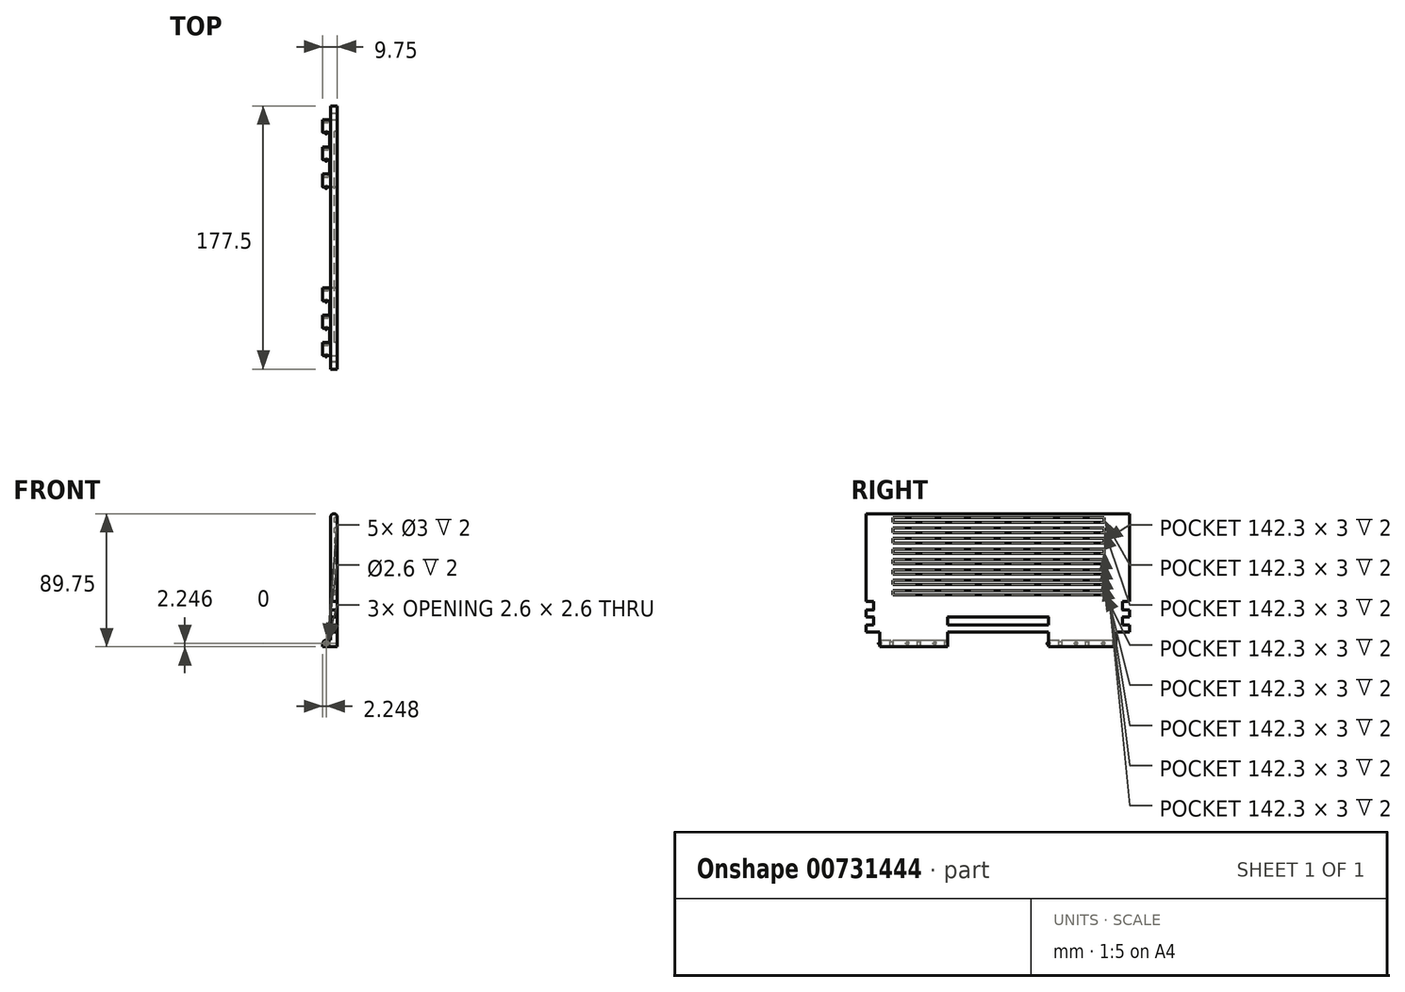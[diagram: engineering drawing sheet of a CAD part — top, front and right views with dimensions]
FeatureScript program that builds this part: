
annotation { "Feature Type Name" : "Feature", "Feature Type Description" : "" }
export const myFeature = defineFeature(function(context is Context, id is Id, definition is map)
    precondition{}
    {
        {
            var Q0;
            Q0=qCreatedBy(makeId("Front.planeOp"),FACE);
            var sketch = newSketch(context, id + "F0", { "sketchPlane" : qUnion([Q0])});
            skLineSegment(sketch, "E0", {"start": v(-23.3, -0.71) * mm, "end": v(-23.3, 86.79) * mm});
            skLineSegment(sketch, "E1", {"start": v(-25.55, 89.04) * mm, "end": v(-25.55, 89.04) * mm});
            skLineSegment(sketch, "E2", {"start": v(-27.8, 86.79) * mm, "end": v(-27.8, 29.79) * mm});
            skLineSegment(sketch, "E3", {"start": v(-33.05, -0.71) * mm, "end": v(-30.8, -0.71) * mm});
            skPoint(sketch, "E4.visualSharp", {"position": v(-28.55, -0.71) * mm});
            skLineSegment(sketch, "E5", {"start": v(-33.05, -0.71) * mm, "end": v(-23.3, -0.71) * mm});
            skLineSegment(sketch, "E6", {"start": v(-33.05, 1.54) * mm, "end": v(-33.05, -0.71) * mm});
            skLineSegment(sketch, "E7", {"start": v(-30.8, 3.79) * mm, "end": v(-27.8, 3.79) * mm});
            skPoint(sketch, "E8.visualSharp", {"position": v(-33.05, 3.79) * mm});
            skArc(sketch, "E8.filletArc", {"start": v(-30.8, 3.79) * mm, "mid": v(-32.4, 3.13) * mm, "end": v(-33.05, 1.54) * mm});
            skCircle(sketch, "E9", {"center": v(-30.8, 1.54) * mm, "radius": 1.5 * mm});
            skCircle(sketch, "E10", {"center": v(-30.8, 1.54) * mm, "radius": 1.3 * mm});
            skPoint(sketch, "E11.visualSharp", {"position": v(-27.8, 89.04) * mm});
            skArc(sketch, "E11.filletArc", {"start": v(-25.55, 89.04) * mm, "mid": v(-27.14, 88.38) * mm, "end": v(-27.8, 86.79) * mm});
            skPoint(sketch, "E12.visualSharp", {"position": v(-23.3, 89.04) * mm});
            skArc(sketch, "E12.filletArc", {"start": v(-23.3, 86.79) * mm, "mid": v(-23.96, 88.38) * mm, "end": v(-25.55, 89.04) * mm});
            skLineSegment(sketch, "E13", {"start": v(-27.8, 9.29) * mm, "end": v(-23.3, 9.29) * mm});
            skLineSegment(sketch, "E14", {"start": v(-28.35, 3.79) * mm, "end": v(-28.35, -0.71) * mm});
            skPoint(sketch, "E14.endSnap0", {"position": v(-28.18, -0.71) * mm});
            skLineSegment(sketch, "E15", {"start": v(-26.8, 24.29) * mm, "end": v(-23.3, 24.29) * mm});
            skLineSegment(sketch, "E16", {"start": v(-27.8, 29.79) * mm, "end": v(-23.3, 29.79) * mm});
            skLineSegment(sketch, "E17.filletArc", {"start": v(-27.8, 29.79) * mm, "end": v(-27.8, 29.79) * mm});
            skLineSegment(sketch, "E18", {"start": v(-27.8, 23.29) * mm, "end": v(-27.8, 20.29) * mm});
            skLineSegment(sketch, "E19", {"start": v(-27.8, 24.29) * mm, "end": v(-27.8, 29.79) * mm});
            skPoint(sketch, "E20.visualSharp", {"position": v(-27.8, 24.29) * mm});
            skArc(sketch, "E20.filletArc", {"start": v(-26.8, 24.29) * mm, "mid": v(-27.5, 24) * mm, "end": v(-27.8, 23.29) * mm});
            skLineSegment(sketch, "E21", {"start": v(-27.8, 24.29) * mm, "end": v(-27.8, 23.29) * mm});
            skLineSegment(sketch, "E22", {"start": v(-23.3, 19.29) * mm, "end": v(-26.8, 19.29) * mm});
            skLineSegment(sketch, "E23", {"start": v(-23.3, 13.89) * mm, "end": v(-27.8, 13.89) * mm});
            skArc(sketch, "E24.filletArc", {"start": v(-27.8, 20.29) * mm, "mid": v(-27.5, 19.58) * mm, "end": v(-26.8, 19.29) * mm});
            skLineSegment(sketch, "E25", {"start": v(-27.8, 13.89) * mm, "end": v(-27.8, 3.79) * mm});
            skLineSegment(sketch, "E26.filletArc", {"start": v(-27.8, 13.89) * mm, "end": v(-27.8, 13.89) * mm});
            skLineSegment(sketch, "E27", {"start": v(-27.8, 20.29) * mm, "end": v(-27.8, 13.89) * mm});
            skSolve(sketch);
        }
        {
            var Q0;
            {var subQ0=sQuery(id+"F0.wireOp",EDGE,"E13");Q0=makeQuery(id+"F0.imprint","IMPRINT",FACE,{"disambiguationData":[TD([[makeQuery(id+"F0.imprint","IMPRINT",EDGE,{"derivedFrom":subQ0}),1.0]])]});}
            var Q1;
            {var subQ3=sQuery(id+"F0.wireOp",EDGE,"E6");Q1=makeQuery(id+"F0.imprint","IMPRINT",FACE,{"disambiguationData":[TD([[makeQuery(id+"F0.imprint","IMPRINT",EDGE,{"derivedFrom":subQ3}),1.0]])]});}
            var Q2;
            {var subQ1=sQuery(id+"F0.wireOp",EDGE,"E11.filletArc");Q2=makeQuery(id+"F0.imprint","IMPRINT",FACE,{"disambiguationData":[TD([[makeQuery(id+"F0.imprint","IMPRINT",EDGE,{"derivedFrom":subQ1}),1.0]])]});}
            var Q3;
            {var subQ0=sQuery(id+"F0.wireOp",EDGE,"E15");Q3=makeQuery(id+"F0.imprint","IMPRINT",FACE,{"disambiguationData":[TD([[makeQuery(id+"F0.imprint","IMPRINT",EDGE,{"derivedFrom":subQ0}),-1.0]])]});}
            extrude(context, id + "F1", {"entities" : qUnion([Q0, Q1, Q2, Q3]), "depth" : 177.5 * mm, "offsetDistance" : 25 * mm});
        }
        {
            var Q0;
            {var subQ0=sQuery(id+"F0.wireOp",EDGE,"cf15f22d-8f12-4429-aff2-0e4cbedbb23c");Q0=makeQuery(id+"F0.imprint","IMPRINT",FACE,{"disambiguationData":[TD([[makeQuery(id+"F0.imprint","IMPRINT",EDGE,{"derivedFrom":subQ0}),1.0]])]});}
            var Q1;
            {var subQ0=sQuery(id+"F0.wireOp",EDGE,"E6");Q1=makeQuery(id+"F0.imprint","IMPRINT",FACE,{"disambiguationData":[TD([[makeQuery(id+"F0.imprint","IMPRINT",EDGE,{"derivedFrom":subQ0}),1.0]])]});}
            extrude(context, id + "F2", {"entities" : qUnion([Q0, Q1]), "operationType" : NewBodyOperationType.REMOVE, "depth" : 177.5 * mm, "offsetDistance" : 25 * mm});
        }
        {
            var Q0;
            {var subQ0=sQuery(id+"F0.wireOp",EDGE,"E6");Q0=makeQuery(id+"F0.imprint","IMPRINT",FACE,{"disambiguationData":[TD([[makeQuery(id+"F0.imprint","IMPRINT",EDGE,{"derivedFrom":subQ0}),1.0]])]});}
            var Q1;
            {var subQ0=sQuery(id+"F0.wireOp",EDGE,"cf15f22d-8f12-4429-aff2-0e4cbedbb23c");Q1=makeQuery(id+"F0.imprint","IMPRINT",FACE,{"disambiguationData":[TD([[makeQuery(id+"F0.imprint","IMPRINT",EDGE,{"derivedFrom":subQ0}),1.0]])]});}
            var Q2;
            {var subQ4=sQuery(id+"F0.wireOp",EDGE,"E13");Q2=makeQuery(id+"F0.imprint","IMPRINT",FACE,{"disambiguationData":[TD([[makeQuery(id+"F0.imprint","IMPRINT",EDGE,{"derivedFrom":subQ4}),-1.0]])]});}
            extrude(context, id + "F3", {"entities" : qUnion([Q0, Q1, Q2]), "operationType" : NewBodyOperationType.ADD, "depth" : 168.3 * mm, "offsetDistance" : 25 * mm});
        }
        {
            var Q0;
            {var subQ0=sQuery(id+"F0.wireOp",EDGE,"E6");Q0=makeQuery(id+"F0.imprint","IMPRINT",FACE,{"disambiguationData":[TD([[makeQuery(id+"F0.imprint","IMPRINT",EDGE,{"derivedFrom":subQ0}),1.0]])]});}
            extrude(context, id + "F4", {"entities" : qUnion([Q0]), "operationType" : NewBodyOperationType.REMOVE, "depth" : 159.5 * mm, "offsetDistance" : 25 * mm});
        }
        {
            var Q0;
            {var subQ0=sQuery(id+"F0.wireOp",EDGE,"cf15f22d-8f12-4429-aff2-0e4cbedbb23c");Q0=makeQuery(id+"F0.imprint","IMPRINT",FACE,{"disambiguationData":[TD([[makeQuery(id+"F0.imprint","IMPRINT",EDGE,{"derivedFrom":subQ0}),1.0]])]});}
            var Q1;
            {var subQ0=sQuery(id+"F0.wireOp",EDGE,"E6");Q1=makeQuery(id+"F0.imprint","IMPRINT",FACE,{"disambiguationData":[TD([[makeQuery(id+"F0.imprint","IMPRINT",EDGE,{"derivedFrom":subQ0}),1.0]])]});}
            var Q2;
            {var subQ4=sQuery(id+"F0.wireOp",EDGE,"E13");Q2=makeQuery(id+"F0.imprint","IMPRINT",FACE,{"disambiguationData":[TD([[makeQuery(id+"F0.imprint","IMPRINT",EDGE,{"derivedFrom":subQ4}),-1.0]])]});}
            extrude(context, id + "F5", {"entities" : qUnion([Q0, Q1, Q2]), "operationType" : NewBodyOperationType.ADD, "depth" : 149.9 * mm, "offsetDistance" : 25 * mm});
        }
        {
            var Q0;
            {var subQ0=sQuery(id+"F0.wireOp",EDGE,"E6");Q0=makeQuery(id+"F0.imprint","IMPRINT",FACE,{"disambiguationData":[TD([[makeQuery(id+"F0.imprint","IMPRINT",EDGE,{"derivedFrom":subQ0}),1.0]])]});}
            extrude(context, id + "F6", {"entities" : qUnion([Q0]), "operationType" : NewBodyOperationType.REMOVE, "depth" : 141.1 * mm, "offsetDistance" : 25 * mm});
        }
        {
            var Q0;
            {var subQ0=sQuery(id+"F0.wireOp",EDGE,"cf15f22d-8f12-4429-aff2-0e4cbedbb23c");Q0=makeQuery(id+"F0.imprint","IMPRINT",FACE,{"disambiguationData":[TD([[makeQuery(id+"F0.imprint","IMPRINT",EDGE,{"derivedFrom":subQ0}),1.0]])]});}
            var Q1;
            {var subQ0=sQuery(id+"F0.wireOp",EDGE,"E6");Q1=makeQuery(id+"F0.imprint","IMPRINT",FACE,{"disambiguationData":[TD([[makeQuery(id+"F0.imprint","IMPRINT",EDGE,{"derivedFrom":subQ0}),1.0]])]});}
            extrude(context, id + "F7", {"entities" : qUnion([Q0, Q1]), "operationType" : NewBodyOperationType.ADD, "depth" : 131.5 * mm, "offsetDistance" : 25 * mm});
        }
        {
            var Q0;
            {var subQ0=sQuery(id+"F0.wireOp",EDGE,"cf15f22d-8f12-4429-aff2-0e4cbedbb23c");Q0=makeQuery(id+"F0.imprint","IMPRINT",FACE,{"disambiguationData":[TD([[makeQuery(id+"F0.imprint","IMPRINT",EDGE,{"derivedFrom":subQ0}),1.0]])]});}
            var Q1;
            {var subQ0=sQuery(id+"F0.wireOp",EDGE,"E6");Q1=makeQuery(id+"F0.imprint","IMPRINT",FACE,{"disambiguationData":[TD([[makeQuery(id+"F0.imprint","IMPRINT",EDGE,{"derivedFrom":subQ0}),1.0]])]});}
            var Q2;
            {var subQ4=sQuery(id+"F0.wireOp",EDGE,"E13");Q2=makeQuery(id+"F0.imprint","IMPRINT",FACE,{"disambiguationData":[TD([[makeQuery(id+"F0.imprint","IMPRINT",EDGE,{"derivedFrom":subQ4}),-1.0]])]});}
            extrude(context, id + "F8", {"entities" : qUnion([Q0, Q1, Q2]), "operationType" : NewBodyOperationType.REMOVE, "depth" : 122.7 * mm, "offsetDistance" : 25 * mm});
        }
        {
            var Q0;
            {var subQ0=sQuery(id+"F0.wireOp",EDGE,"cf15f22d-8f12-4429-aff2-0e4cbedbb23c");Q0=makeQuery(id+"F0.imprint","IMPRINT",FACE,{"disambiguationData":[TD([[makeQuery(id+"F0.imprint","IMPRINT",EDGE,{"derivedFrom":subQ0}),1.0]])]});}
            var Q1;
            {var subQ0=sQuery(id+"F0.wireOp",EDGE,"E6");Q1=makeQuery(id+"F0.imprint","IMPRINT",FACE,{"disambiguationData":[TD([[makeQuery(id+"F0.imprint","IMPRINT",EDGE,{"derivedFrom":subQ0}),1.0]])]});}
            var Q2;
            {var subQ4=sQuery(id+"F0.wireOp",EDGE,"E13");Q2=makeQuery(id+"F0.imprint","IMPRINT",FACE,{"disambiguationData":[TD([[makeQuery(id+"F0.imprint","IMPRINT",EDGE,{"derivedFrom":subQ4}),-1.0]])]});}
            extrude(context, id + "F9", {"entities" : qUnion([Q0, Q1, Q2]), "operationType" : NewBodyOperationType.ADD, "depth" : 54.8 * mm, "offsetDistance" : 25 * mm});
        }
        {
            var Q0;
            {var subQ0=sQuery(id+"F0.wireOp",EDGE,"E6");Q0=makeQuery(id+"F0.imprint","IMPRINT",FACE,{"disambiguationData":[TD([[makeQuery(id+"F0.imprint","IMPRINT",EDGE,{"derivedFrom":subQ0}),1.0]])]});}
            extrude(context, id + "F10", {"entities" : qUnion([Q0]), "operationType" : NewBodyOperationType.REMOVE, "depth" : 46 * mm, "offsetDistance" : 25 * mm});
        }
        {
            var Q0;
            {var subQ0=sQuery(id+"F0.wireOp",EDGE,"cf15f22d-8f12-4429-aff2-0e4cbedbb23c");Q0=makeQuery(id+"F0.imprint","IMPRINT",FACE,{"disambiguationData":[TD([[makeQuery(id+"F0.imprint","IMPRINT",EDGE,{"derivedFrom":subQ0}),1.0]])]});}
            var Q1;
            {var subQ0=sQuery(id+"F0.wireOp",EDGE,"E6");Q1=makeQuery(id+"F0.imprint","IMPRINT",FACE,{"disambiguationData":[TD([[makeQuery(id+"F0.imprint","IMPRINT",EDGE,{"derivedFrom":subQ0}),1.0]])]});}
            extrude(context, id + "F11", {"entities" : qUnion([Q0, Q1]), "operationType" : NewBodyOperationType.ADD, "depth" : 36.4 * mm, "offsetDistance" : 25 * mm});
        }
        {
            var Q0;
            {var subQ0=sQuery(id+"F0.wireOp",EDGE,"E6");Q0=makeQuery(id+"F0.imprint","IMPRINT",FACE,{"disambiguationData":[TD([[makeQuery(id+"F0.imprint","IMPRINT",EDGE,{"derivedFrom":subQ0}),1.0]])]});}
            extrude(context, id + "F12", {"entities" : qUnion([Q0]), "operationType" : NewBodyOperationType.REMOVE, "depth" : 27.6 * mm, "offsetDistance" : 25 * mm});
        }
        {
            var Q0;
            {var subQ0=sQuery(id+"F0.wireOp",EDGE,"cf15f22d-8f12-4429-aff2-0e4cbedbb23c");Q0=makeQuery(id+"F0.imprint","IMPRINT",FACE,{"disambiguationData":[TD([[makeQuery(id+"F0.imprint","IMPRINT",EDGE,{"derivedFrom":subQ0}),1.0]])]});}
            var Q1;
            {var subQ0=sQuery(id+"F0.wireOp",EDGE,"E6");Q1=makeQuery(id+"F0.imprint","IMPRINT",FACE,{"disambiguationData":[TD([[makeQuery(id+"F0.imprint","IMPRINT",EDGE,{"derivedFrom":subQ0}),1.0]])]});}
            extrude(context, id + "F13", {"entities" : qUnion([Q0, Q1]), "operationType" : NewBodyOperationType.ADD, "depth" : 18 * mm, "offsetDistance" : 25 * mm});
        }
        {
            var Q0;
            {var subQ0=sQuery(id+"F0.wireOp",EDGE,"cf15f22d-8f12-4429-aff2-0e4cbedbb23c");Q0=makeQuery(id+"F0.imprint","IMPRINT",FACE,{"disambiguationData":[TD([[makeQuery(id+"F0.imprint","IMPRINT",EDGE,{"derivedFrom":subQ0}),1.0]])]});}
            var Q1;
            {var subQ0=sQuery(id+"F0.wireOp",EDGE,"E6");Q1=makeQuery(id+"F0.imprint","IMPRINT",FACE,{"disambiguationData":[TD([[makeQuery(id+"F0.imprint","IMPRINT",EDGE,{"derivedFrom":subQ0}),1.0]])]});}
            var Q2;
            {var subQ4=sQuery(id+"F0.wireOp",EDGE,"E13");Q2=makeQuery(id+"F0.imprint","IMPRINT",FACE,{"disambiguationData":[TD([[makeQuery(id+"F0.imprint","IMPRINT",EDGE,{"derivedFrom":subQ4}),-1.0]])]});}
            var Q3;
            {var subQ0=sQuery(id+"F0.wireOp",EDGE,"E22");Q3=makeQuery(id+"F0.imprint","IMPRINT",FACE,{"disambiguationData":[TD([[makeQuery(id+"F0.imprint","IMPRINT",EDGE,{"derivedFrom":subQ0}),1.0]])]});}
            extrude(context, id + "F14", {"entities" : qUnion([Q0, Q1, Q2, Q3]), "operationType" : NewBodyOperationType.REMOVE, "depth" : 9.2 * mm, "offsetDistance" : 25 * mm});
        }
        {
            var Q0;
            {var subQ0=sQuery(id+"F0.wireOp",EDGE,"E15");Q0=makeQuery(id+"F0.imprint","IMPRINT",FACE,{"disambiguationData":[TD([[makeQuery(id+"F0.imprint","IMPRINT",EDGE,{"derivedFrom":subQ0}),1.0]])]});}
            var Q1;
            {var subQ0=sQuery(id+"F0.wireOp",EDGE,"E22");Q1=makeQuery(id+"F0.imprint","IMPRINT",FACE,{"disambiguationData":[TD([[makeQuery(id+"F0.imprint","IMPRINT",EDGE,{"derivedFrom":subQ0}),1.0]])]});}
            extrude(context, id + "F15", {"entities" : qUnion([Q0, Q1]), "operationType" : NewBodyOperationType.ADD, "depth" : 172.6 * mm, "offsetDistance" : 25 * mm});
        }
        {
            var Q0;
            {var subQ1=sQuery(id+"F0.wireOp",EDGE,"E15");Q0=makeQuery(id+"F0.imprint","IMPRINT",FACE,{"disambiguationData":[TD([[makeQuery(id+"F0.imprint","IMPRINT",EDGE,{"derivedFrom":subQ1}),1.0]])]});}
            var Q1;
            {var subQ0=sQuery(id+"F0.wireOp",EDGE,"E22");Q1=makeQuery(id+"F0.imprint","IMPRINT",FACE,{"disambiguationData":[TD([[makeQuery(id+"F0.imprint","IMPRINT",EDGE,{"derivedFrom":subQ0}),1.0]])]});}
            extrude(context, id + "F16", {"entities" : qUnion([Q0, Q1]), "operationType" : NewBodyOperationType.REMOVE, "depth" : 4.7 * mm, "offsetDistance" : 25 * mm});
        }
        {
            var Q0;
            {var subQ1=sQuery(id+"F0.wireOp",EDGE,"E22");Q0=makeQuery(id+"F0.imprint","IMPRINT",FACE,{"disambiguationData":[TD([[makeQuery(id+"F0.imprint","IMPRINT",EDGE,{"derivedFrom":subQ1}),1.0]])]});}
            extrude(context, id + "F17", {"entities" : qUnion([Q0]), "operationType" : NewBodyOperationType.REMOVE, "depth" : 122.7 * mm, "offsetDistance" : 25 * mm});
        }
        {
            var Q0;
            {var subQ1=sQuery(id+"F0.wireOp",EDGE,"E22");Q0=makeQuery(id+"F0.imprint","IMPRINT",FACE,{"disambiguationData":[TD([[makeQuery(id+"F0.imprint","IMPRINT",EDGE,{"derivedFrom":subQ1}),1.0]])]});}
            extrude(context, id + "F18", {"entities" : qUnion([Q0]), "operationType" : NewBodyOperationType.ADD, "depth" : 54.8 * mm, "offsetDistance" : 25 * mm});
        }
        {
            var Q0;
            {var subQ1=sQuery(id+"F0.wireOp",EDGE,"E22");Q0=makeQuery(id+"F0.imprint","IMPRINT",FACE,{"disambiguationData":[TD([[makeQuery(id+"F0.imprint","IMPRINT",EDGE,{"derivedFrom":subQ1}),1.0]])]});}
            var Q1;
            {var subQ1=sQuery(id+"F0.wireOp",EDGE,"E15");Q1=makeQuery(id+"F0.imprint","IMPRINT",FACE,{"disambiguationData":[TD([[makeQuery(id+"F0.imprint","IMPRINT",EDGE,{"derivedFrom":subQ1}),1.0]])]});}
            extrude(context, id + "F19", {"entities" : qUnion([Q0, Q1]), "operationType" : NewBodyOperationType.REMOVE, "depth" : 4.9 * mm, "offsetDistance" : 25 * mm});
        }
        {
            var Q0;
            Q0=makeQuery(id+"F14.boolean.opBoolean","COPY",FACE,{"derivedFrom":makeQuery(id+"F14.opExtrude","CAP_FACE",FACE,{"disambiguationData":[OSD([sQuery(id+"F0.wireOp",EDGE,"E0"),sQuery(id+"F0.wireOp",EDGE,"E5"),sQuery(id+"F0.wireOp",EDGE,"E6"),sQuery(id+"F0.wireOp",EDGE,"E7"),sQuery(id+"F0.wireOp",EDGE,"E8.filletArc"),sQuery(id+"F0.wireOp",EDGE,"E9"),sQuery(id+"F0.wireOp",EDGE,"E13"),sQuery(id+"F0.wireOp",EDGE,"E25")])],"isStart":false})});
            var sketch = newSketch(context, id + "F20", { "sketchPlane" : qUnion([Q0])});
            skCircle(sketch, "E28", {"center": v(30.8, 1.54) * mm, "radius": 1.3 * mm});
            skCircle(sketch, "E29", {"center": v(30.8, 1.54) * mm, "radius": 1.5 * mm});
            skSolve(sketch);
        }
        {
            var Q0;
            Q0=makeQuery(id+"F12.boolean.opBoolean","COPY",FACE,{"derivedFrom":makeQuery(id+"F12.opExtrude","CAP_FACE",FACE,{"disambiguationData":[OSD([sQuery(id+"F0.wireOp",EDGE,"E5"),sQuery(id+"F0.wireOp",EDGE,"E6"),sQuery(id+"F0.wireOp",EDGE,"E7"),sQuery(id+"F0.wireOp",EDGE,"E8.filletArc"),sQuery(id+"F0.wireOp",EDGE,"E9"),sQuery(id+"F0.wireOp",EDGE,"E14")])],"isStart":false})});
            var sketch = newSketch(context, id + "F21", { "sketchPlane" : qUnion([Q0])});
            skCircle(sketch, "E30", {"center": v(30.8, 1.54) * mm, "radius": 1.5 * mm});
            skCircle(sketch, "E31", {"center": v(30.8, 1.54) * mm, "radius": 1.3 * mm});
            skSolve(sketch);
        }
        {
            var Q0;
            Q0=makeQuery(id+"F10.boolean.opBoolean","COPY",FACE,{"derivedFrom":makeQuery(id+"F10.opExtrude","CAP_FACE",FACE,{"disambiguationData":[OSD([sQuery(id+"F0.wireOp",EDGE,"E5"),sQuery(id+"F0.wireOp",EDGE,"E6"),sQuery(id+"F0.wireOp",EDGE,"E7"),sQuery(id+"F0.wireOp",EDGE,"E8.filletArc"),sQuery(id+"F0.wireOp",EDGE,"E9"),sQuery(id+"F0.wireOp",EDGE,"E14")])],"isStart":false})});
            var sketch = newSketch(context, id + "F22", { "sketchPlane" : qUnion([Q0])});
            skCircle(sketch, "E32", {"center": v(30.8, 1.54) * mm, "radius": 1.3 * mm});
            skCircle(sketch, "E33", {"center": v(30.8, 1.54) * mm, "radius": 1.5 * mm});
            skSolve(sketch);
        }
        {
            var Q0;
            Q0=makeQuery(id+"F8.boolean.opBoolean","COPY",FACE,{"derivedFrom":makeQuery(id+"F8.opExtrude","CAP_FACE",FACE,{"disambiguationData":[OSD([sQuery(id+"F0.wireOp",EDGE,"E0"),sQuery(id+"F0.wireOp",EDGE,"E5"),sQuery(id+"F0.wireOp",EDGE,"E6"),sQuery(id+"F0.wireOp",EDGE,"E7"),sQuery(id+"F0.wireOp",EDGE,"E8.filletArc"),sQuery(id+"F0.wireOp",EDGE,"E9"),sQuery(id+"F0.wireOp",EDGE,"E13"),sQuery(id+"F0.wireOp",EDGE,"E25")])],"isStart":false})});
            var sketch = newSketch(context, id + "F23", { "sketchPlane" : qUnion([Q0])});
            skCircle(sketch, "E34", {"center": v(30.8, 1.54) * mm, "radius": 1.3 * mm});
            skCircle(sketch, "E35", {"center": v(30.8, 1.54) * mm, "radius": 1.5 * mm});
            skSolve(sketch);
        }
        {
            var Q0;
            Q0=makeQuery(id+"F6.boolean.opBoolean","COPY",FACE,{"derivedFrom":makeQuery(id+"F6.opExtrude","CAP_FACE",FACE,{"disambiguationData":[OSD([sQuery(id+"F0.wireOp",EDGE,"E5"),sQuery(id+"F0.wireOp",EDGE,"E6"),sQuery(id+"F0.wireOp",EDGE,"E7"),sQuery(id+"F0.wireOp",EDGE,"E8.filletArc"),sQuery(id+"F0.wireOp",EDGE,"E9"),sQuery(id+"F0.wireOp",EDGE,"E14")])],"isStart":false})});
            var sketch = newSketch(context, id + "F24", { "sketchPlane" : qUnion([Q0])});
            skCircle(sketch, "E36", {"center": v(30.8, 1.54) * mm, "radius": 1.3 * mm});
            skCircle(sketch, "E37", {"center": v(30.8, 1.54) * mm, "radius": 1.5 * mm});
            skSolve(sketch);
        }
        {
            var Q0;
            Q0=makeQuery(id+"F4.boolean.opBoolean","COPY",FACE,{"derivedFrom":makeQuery(id+"F4.opExtrude","CAP_FACE",FACE,{"disambiguationData":[OSD([sQuery(id+"F0.wireOp",EDGE,"E5"),sQuery(id+"F0.wireOp",EDGE,"E6"),sQuery(id+"F0.wireOp",EDGE,"E7"),sQuery(id+"F0.wireOp",EDGE,"E8.filletArc"),sQuery(id+"F0.wireOp",EDGE,"E9"),sQuery(id+"F0.wireOp",EDGE,"E14")])],"isStart":false})});
            var sketch = newSketch(context, id + "F25", { "sketchPlane" : qUnion([Q0])});
            skCircle(sketch, "E38", {"center": v(30.8, 1.54) * mm, "radius": 1.3 * mm});
            skCircle(sketch, "E39", {"center": v(30.8, 1.54) * mm, "radius": 1.5 * mm});
            skSolve(sketch);
        }
        {
            var Q0;
            Q0=makeQuery(id+"F20.imprint","IMPRINT",FACE,{"disambiguationData":[TD([[makeQuery(id+"F20.imprint","IMPRINT",EDGE,{"derivedFrom":sQuery(id+"F20.wireOp",EDGE,"E28")}),-1.0]])]});
            var Q1;
            Q1=makeQuery(id+"F21.imprint","IMPRINT",FACE,{"disambiguationData":[TD([[makeQuery(id+"F21.imprint","IMPRINT",EDGE,{"derivedFrom":sQuery(id+"F21.wireOp",EDGE,"E30")}),-1.0]])]});
            var Q2;
            Q2=makeQuery(id+"F22.imprint","IMPRINT",FACE,{"disambiguationData":[TD([[makeQuery(id+"F22.imprint","IMPRINT",EDGE,{"derivedFrom":sQuery(id+"F22.wireOp",EDGE,"E32")}),-1.0]])]});
            var Q3;
            Q3=makeQuery(id+"F23.imprint","IMPRINT",FACE,{"disambiguationData":[TD([[makeQuery(id+"F23.imprint","IMPRINT",EDGE,{"derivedFrom":sQuery(id+"F23.wireOp",EDGE,"E34")}),-1.0]])]});
            var Q4;
            Q4=makeQuery(id+"F24.imprint","IMPRINT",FACE,{"disambiguationData":[TD([[makeQuery(id+"F24.imprint","IMPRINT",EDGE,{"derivedFrom":sQuery(id+"F24.wireOp",EDGE,"E36")}),-1.0]])]});
            var Q5;
            Q5=makeQuery(id+"F25.imprint","IMPRINT",FACE,{"disambiguationData":[TD([[makeQuery(id+"F25.imprint","IMPRINT",EDGE,{"derivedFrom":sQuery(id+"F25.wireOp",EDGE,"E38")}),-1.0]])]});
            extrude(context, id + "F26", {"entities" : qUnion([Q0, Q1, Q2, Q3, Q4, Q5]), "operationType" : NewBodyOperationType.ADD, "oppositeDirection" : true, "depth" : 8.8 * mm, "offsetDistance" : 25 * mm});
        }
        {
            var Q0;
            Q0=makeQuery(id+"F20.imprint","IMPRINT",FACE,{"disambiguationData":[TD([[makeQuery(id+"F20.imprint","IMPRINT",EDGE,{"derivedFrom":sQuery(id+"F20.wireOp",EDGE,"E28")}),1.0]])]});
            var Q1;
            Q1=makeQuery(id+"F21.imprint","IMPRINT",FACE,{"disambiguationData":[TD([[makeQuery(id+"F21.imprint","IMPRINT",EDGE,{"derivedFrom":sQuery(id+"F21.wireOp",EDGE,"E31")}),1.0]])]});
            var Q2;
            Q2=makeQuery(id+"F22.imprint","IMPRINT",FACE,{"disambiguationData":[TD([[makeQuery(id+"F22.imprint","IMPRINT",EDGE,{"derivedFrom":sQuery(id+"F22.wireOp",EDGE,"E32")}),1.0]])]});
            var Q3;
            Q3=makeQuery(id+"F23.imprint","IMPRINT",FACE,{"disambiguationData":[TD([[makeQuery(id+"F23.imprint","IMPRINT",EDGE,{"derivedFrom":sQuery(id+"F23.wireOp",EDGE,"E34")}),1.0]])]});
            var Q4;
            Q4=makeQuery(id+"F24.imprint","IMPRINT",FACE,{"disambiguationData":[TD([[makeQuery(id+"F24.imprint","IMPRINT",EDGE,{"derivedFrom":sQuery(id+"F24.wireOp",EDGE,"E36")}),1.0]])]});
            var Q5;
            Q5=makeQuery(id+"F25.imprint","IMPRINT",FACE,{"disambiguationData":[TD([[makeQuery(id+"F25.imprint","IMPRINT",EDGE,{"derivedFrom":sQuery(id+"F25.wireOp",EDGE,"E38")}),1.0]])]});
            extrude(context, id + "F27", {"entities" : qUnion([Q0, Q1, Q2, Q3, Q4, Q5]), "operationType" : NewBodyOperationType.ADD, "oppositeDirection" : true, "depth" : 9.8 * mm, "offsetDistance" : 25 * mm});
        }
        {
            var Q0;
            Q0=makeQuery(id+"F20.imprint","IMPRINT",FACE,{"disambiguationData":[TD([[makeQuery(id+"F20.imprint","IMPRINT",EDGE,{"derivedFrom":sQuery(id+"F20.wireOp",EDGE,"E28")}),-1.0]])]});
            var Q1;
            Q1=makeQuery(id+"F20.imprint","IMPRINT",FACE,{"disambiguationData":[TD([[makeQuery(id+"F20.imprint","IMPRINT",EDGE,{"derivedFrom":sQuery(id+"F20.wireOp",EDGE,"E28")}),1.0]])]});
            var Q2;
            Q2=makeQuery(id+"F21.imprint","IMPRINT",FACE,{"disambiguationData":[TD([[makeQuery(id+"F21.imprint","IMPRINT",EDGE,{"derivedFrom":sQuery(id+"F21.wireOp",EDGE,"E30")}),-1.0]])]});
            var Q3;
            Q3=makeQuery(id+"F21.imprint","IMPRINT",FACE,{"disambiguationData":[TD([[makeQuery(id+"F21.imprint","IMPRINT",EDGE,{"derivedFrom":sQuery(id+"F21.wireOp",EDGE,"E31")}),1.0]])]});
            var Q4;
            Q4=makeQuery(id+"F22.imprint","IMPRINT",FACE,{"disambiguationData":[TD([[makeQuery(id+"F22.imprint","IMPRINT",EDGE,{"derivedFrom":sQuery(id+"F22.wireOp",EDGE,"E32")}),1.0]])]});
            var Q5;
            Q5=makeQuery(id+"F23.imprint","IMPRINT",FACE,{"disambiguationData":[TD([[makeQuery(id+"F23.imprint","IMPRINT",EDGE,{"derivedFrom":sQuery(id+"F23.wireOp",EDGE,"E34")}),1.0]])]});
            var Q6;
            Q6=makeQuery(id+"F23.imprint","IMPRINT",FACE,{"disambiguationData":[TD([[makeQuery(id+"F23.imprint","IMPRINT",EDGE,{"derivedFrom":sQuery(id+"F23.wireOp",EDGE,"E34")}),-1.0]])]});
            var Q7;
            Q7=makeQuery(id+"F24.imprint","IMPRINT",FACE,{"disambiguationData":[TD([[makeQuery(id+"F24.imprint","IMPRINT",EDGE,{"derivedFrom":sQuery(id+"F24.wireOp",EDGE,"E36")}),-1.0]])]});
            var Q8;
            Q8=makeQuery(id+"F24.imprint","IMPRINT",FACE,{"disambiguationData":[TD([[makeQuery(id+"F24.imprint","IMPRINT",EDGE,{"derivedFrom":sQuery(id+"F24.wireOp",EDGE,"E36")}),1.0]])]});
            var Q9;
            Q9=makeQuery(id+"F25.imprint","IMPRINT",FACE,{"disambiguationData":[TD([[makeQuery(id+"F25.imprint","IMPRINT",EDGE,{"derivedFrom":sQuery(id+"F25.wireOp",EDGE,"E38")}),1.0]])]});
            var Q10;
            Q10=makeQuery(id+"F25.imprint","IMPRINT",FACE,{"disambiguationData":[TD([[makeQuery(id+"F25.imprint","IMPRINT",EDGE,{"derivedFrom":sQuery(id+"F25.wireOp",EDGE,"E38")}),-1.0]])]});
            extrude(context, id + "F28", {"entities" : qUnion([Q0, Q1, Q2, Q3, Q4, Q5, Q6, Q7, Q8, Q9, Q10]), "operationType" : NewBodyOperationType.REMOVE, "oppositeDirection" : true, "depth" : 2 * mm, "offsetDistance" : 25 * mm});
        }
        {
            var Q0;
            Q0=makeQuery(id+"F27.opExtrude","CAP_EDGE",EDGE,{"disambiguationData":[OSD([sQuery(id+"F20.wireOp",EDGE,"E28")])],"isStart":false});
            var Q1;
            Q1=makeQuery(id+"F27.opExtrude","CAP_EDGE",EDGE,{"disambiguationData":[OSD([sQuery(id+"F21.wireOp",EDGE,"E31")])],"isStart":false});
            var Q2;
            Q2=makeQuery(id+"F27.opExtrude","CAP_EDGE",EDGE,{"disambiguationData":[OSD([sQuery(id+"F22.wireOp",EDGE,"E32")])],"isStart":false});
            var Q3;
            Q3=makeQuery(id+"F27.opExtrude","CAP_EDGE",EDGE,{"disambiguationData":[OSD([sQuery(id+"F23.wireOp",EDGE,"E34")])],"isStart":false});
            var Q4;
            Q4=makeQuery(id+"F27.opExtrude","CAP_EDGE",EDGE,{"disambiguationData":[OSD([sQuery(id+"F24.wireOp",EDGE,"E36")])],"isStart":false});
            var Q5;
            Q5=makeQuery(id+"F27.opExtrude","CAP_EDGE",EDGE,{"disambiguationData":[OSD([sQuery(id+"F25.wireOp",EDGE,"E38")])],"isStart":false});
            fillet(context, id + "F29", {"entities" : qUnion([Q0, Q1, Q2, Q3, Q4, Q5]), "radius" : 1 * mm, "tangentPropagation" : true, "allowEdgeOverflow" : false});
        }
        {
            var Q0;
            Q0=qCreatedBy(makeId("Front.planeOp"),FACE);
            cPlane(context, id + "F30", {"entities" : qUnion([Q0]), "cplaneType" : CPlaneType.OFFSET, "offset" : 17.2 * mm, "width" : 150 * mm, "height" : 150 * mm});
        }
        {
            var Q0;
            Q0=qCreatedBy(id+"F30.planeOp",FACE);
            var sketch = newSketch(context, id + "F31", { "sketchPlane" : qUnion([Q0])});
            skLineSegment(sketch, "E40.bottom", {"start": v(-23.3, 72.29) * mm, "end": v(-25.3, 72.29) * mm});
            skLineSegment(sketch, "E40.top", {"start": v(-23.3, 69.29) * mm, "end": v(-25.3, 69.29) * mm});
            skLineSegment(sketch, "E40.left", {"start": v(-23.3, 72.29) * mm, "end": v(-23.3, 69.29) * mm});
            skLineSegment(sketch, "E40.right", {"start": v(-25.3, 72.29) * mm, "end": v(-25.3, 69.29) * mm});
            skLineSegment(sketch, "E41.bottom", {"start": v(-23.3, 65.29) * mm, "end": v(-25.3, 65.29) * mm});
            skLineSegment(sketch, "E41.top", {"start": v(-23.3, 62.29) * mm, "end": v(-25.3, 62.29) * mm});
            skLineSegment(sketch, "E41.left", {"start": v(-23.3, 65.29) * mm, "end": v(-23.3, 62.29) * mm});
            skLineSegment(sketch, "E41.right", {"start": v(-25.3, 65.29) * mm, "end": v(-25.3, 62.29) * mm});
            skLineSegment(sketch, "E42.bottom", {"start": v(-23.3, 58.29) * mm, "end": v(-25.3, 58.29) * mm});
            skLineSegment(sketch, "E42.top", {"start": v(-23.3, 55.29) * mm, "end": v(-25.3, 55.29) * mm});
            skLineSegment(sketch, "E42.left", {"start": v(-23.3, 58.29) * mm, "end": v(-23.3, 55.29) * mm});
            skLineSegment(sketch, "E42.right", {"start": v(-25.3, 58.29) * mm, "end": v(-25.3, 55.29) * mm});
            skLineSegment(sketch, "E43.bottom", {"start": v(-23.3, 51.29) * mm, "end": v(-25.3, 51.29) * mm});
            skLineSegment(sketch, "E43.top", {"start": v(-23.3, 48.29) * mm, "end": v(-25.3, 48.29) * mm});
            skLineSegment(sketch, "E43.left", {"start": v(-23.3, 51.29) * mm, "end": v(-23.3, 48.29) * mm});
            skLineSegment(sketch, "E43.right", {"start": v(-25.3, 51.29) * mm, "end": v(-25.3, 48.29) * mm});
            skLineSegment(sketch, "E44.bottom", {"start": v(-23.3, 44.29) * mm, "end": v(-25.3, 44.29) * mm});
            skLineSegment(sketch, "E44.top", {"start": v(-23.3, 41.29) * mm, "end": v(-25.3, 41.29) * mm});
            skLineSegment(sketch, "E44.left", {"start": v(-23.3, 44.29) * mm, "end": v(-23.3, 41.29) * mm});
            skLineSegment(sketch, "E44.right", {"start": v(-25.3, 44.29) * mm, "end": v(-25.3, 41.29) * mm});
            skLineSegment(sketch, "E45.bottom", {"start": v(-23.3, 37.29) * mm, "end": v(-25.3, 37.29) * mm});
            skLineSegment(sketch, "E45.top", {"start": v(-23.3, 34.29) * mm, "end": v(-25.3, 34.29) * mm});
            skLineSegment(sketch, "E45.left", {"start": v(-23.3, 37.29) * mm, "end": v(-23.3, 34.29) * mm});
            skLineSegment(sketch, "E45.right", {"start": v(-25.3, 37.29) * mm, "end": v(-25.3, 34.29) * mm});
            skLineSegment(sketch, "E46.bottom", {"start": v(-23.3, 76.29) * mm, "end": v(-25.3, 76.29) * mm});
            skLineSegment(sketch, "E46.top", {"start": v(-23.3, 79.29) * mm, "end": v(-25.3, 79.29) * mm});
            skLineSegment(sketch, "E46.left", {"start": v(-23.3, 76.29) * mm, "end": v(-23.3, 79.29) * mm});
            skLineSegment(sketch, "E46.right", {"start": v(-25.3, 76.29) * mm, "end": v(-25.3, 79.29) * mm});
            skLineSegment(sketch, "E47.bottom", {"start": v(-23.3, 83.29) * mm, "end": v(-25.3, 83.29) * mm});
            skLineSegment(sketch, "E47.top", {"start": v(-23.3, 86.29) * mm, "end": v(-25.3, 86.29) * mm});
            skLineSegment(sketch, "E47.left", {"start": v(-23.3, 83.29) * mm, "end": v(-23.3, 86.29) * mm});
            skLineSegment(sketch, "E47.right", {"start": v(-25.3, 83.29) * mm, "end": v(-25.3, 86.29) * mm});
            skSolve(sketch);
        }
        {
            var Q0;
            Q0 = qSketchRegion(id + "F31", true);
            extrude(context, id + "F32", {"entities" : qUnion([Q0]), "operationType" : NewBodyOperationType.REMOVE, "depth" : 142.3 * mm, "offsetDistance" : 25 * mm});
        }
    });
